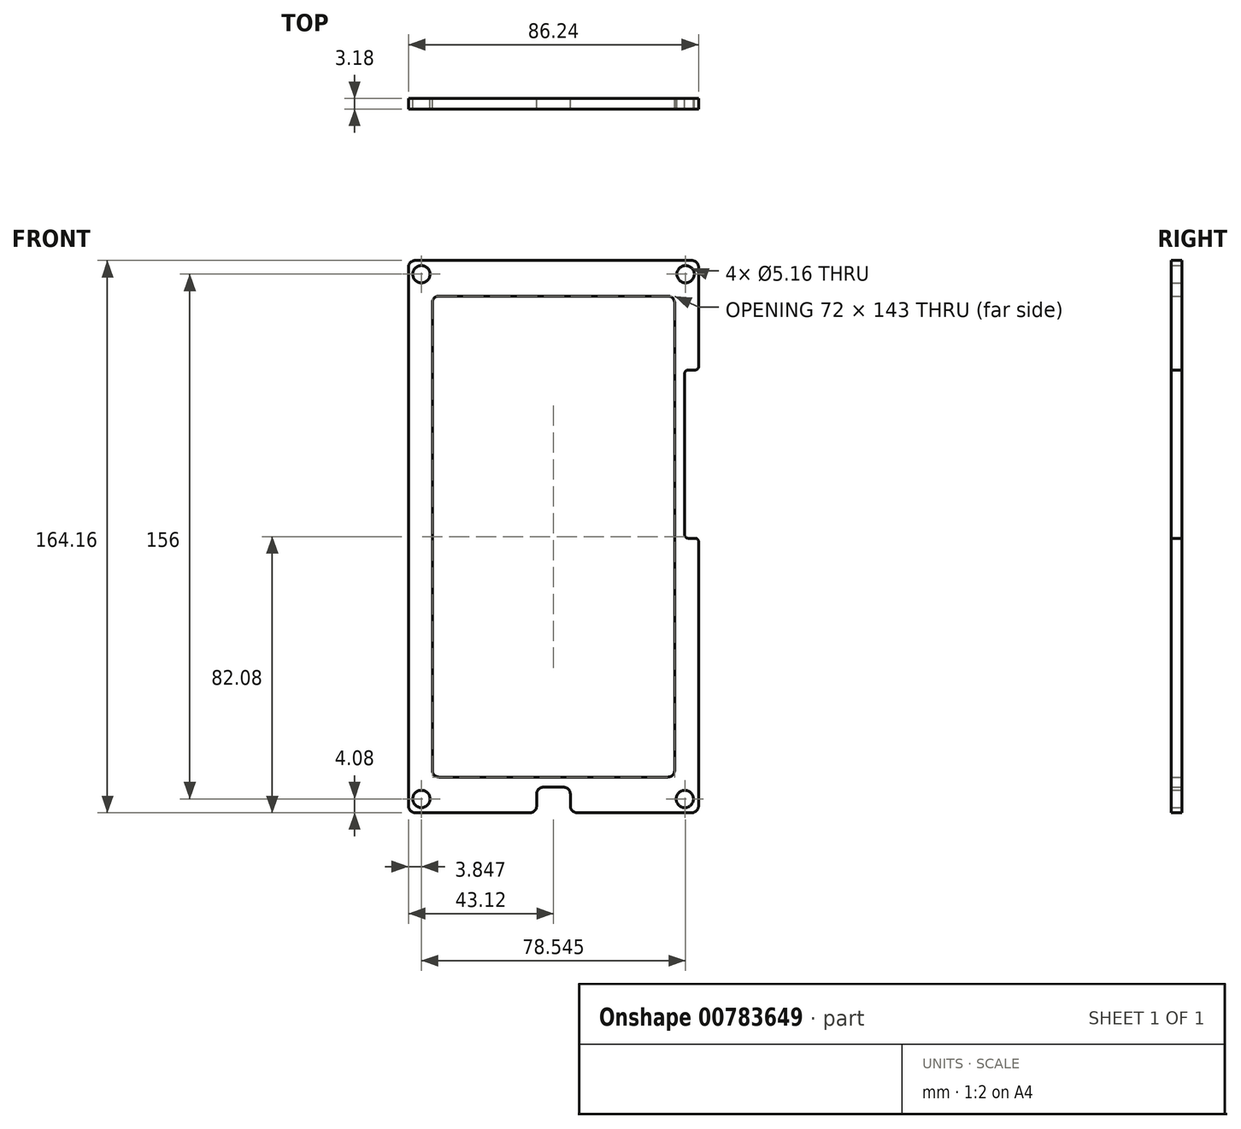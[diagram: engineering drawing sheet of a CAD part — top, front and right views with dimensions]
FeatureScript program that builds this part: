
annotation { "Feature Type Name" : "Feature", "Feature Type Description" : "" }
export const myFeature = defineFeature(function(context is Context, id is Id, definition is map)
    precondition{}
    {
        {
            var Q0;
            Q0=qCreatedBy(makeId("Front.planeOp"),FACE);
            var sketch = newSketch(context, id + "F0", { "sketchPlane" : qUnion([Q0])});
            skLineSegment(sketch, "E0.bottom", {"start": v(39, 74.5) * mm, "end": v(-39, 74.5) * mm});
            skLineSegment(sketch, "E0.top", {"start": v(39, -74.5) * mm, "end": v(-39, -74.5) * mm});
            skLineSegment(sketch, "E0.left", {"start": v(39, 74.5) * mm, "end": v(39, -74.5) * mm});
            skLineSegment(sketch, "E0.right", {"start": v(-39, 74.5) * mm, "end": v(-39, -74.5) * mm});
            skPoint(sketch, "E0.middle", {"position": v(0, 0) * mm});
            skSolve(sketch);
        }
        {
            var Q0;
            Q0=qCreatedBy(makeId("Front.planeOp"),FACE);
            var sketch = newSketch(context, id + "F1", { "sketchPlane" : qUnion([Q0])});
            skLineSegment(sketch, "E1.bottom", {"start": v(34, 71.5) * mm, "end": v(-34, 71.5) * mm});
            skLineSegment(sketch, "E1.top", {"start": v(34, -71.5) * mm, "end": v(-34, -71.5) * mm});
            skLineSegment(sketch, "E1.left", {"start": v(36, 69.5) * mm, "end": v(36, -69.5) * mm});
            skLineSegment(sketch, "E1.right", {"start": v(-36, 69.5) * mm, "end": v(-36, -69.5) * mm});
            skPoint(sketch, "E1.middle", {"position": v(0, 0) * mm});
            skCircle(sketch, "E2", {"center": v(39.27, 78) * mm, "radius": 2.58 * mm});
            skCircle(sketch, "E3", {"center": v(-39.27, 78) * mm, "radius": 2.58 * mm});
            skCircle(sketch, "E4", {"center": v(39.04, -78) * mm, "radius": 2.58 * mm});
            skCircle(sketch, "E5", {"center": v(-39.27, -78) * mm, "radius": 2.58 * mm});
            skLineSegment(sketch, "E6.bottom", {"start": v(41.12, 82.08) * mm, "end": v(-41.12, 82.08) * mm});
            skLineSegment(sketch, "E6.top", {"start": v(41.12, -82.08) * mm, "end": v(7, -82.08) * mm});
            skLineSegment(sketch, "E6.left", {"start": v(43.12, 80.08) * mm, "end": v(43.12, 50.5) * mm});
            skLineSegment(sketch, "E6.right", {"start": v(-43.12, 80.08) * mm, "end": v(-43.12, -80.08) * mm});
            skPoint(sketch, "E7.visualSharp", {"position": v(-36, 71.5) * mm});
            skArc(sketch, "E7.filletArc", {"start": v(-34, 71.5) * mm, "mid": v(-35.41, 70.91) * mm, "end": v(-36, 69.5) * mm});
            skPoint(sketch, "E8.visualSharp", {"position": v(36, 71.5) * mm});
            skArc(sketch, "E8.filletArc", {"start": v(36, 69.5) * mm, "mid": v(35.41, 70.91) * mm, "end": v(34, 71.5) * mm});
            skPoint(sketch, "E9.visualSharp", {"position": v(43.12, 82.08) * mm});
            skArc(sketch, "E9.filletArc", {"start": v(43.12, 80.08) * mm, "mid": v(42.53, 81.5) * mm, "end": v(41.12, 82.08) * mm});
            skPoint(sketch, "E10.visualSharp", {"position": v(-43.12, 82.08) * mm});
            skArc(sketch, "E10.filletArc", {"start": v(-41.12, 82.08) * mm, "mid": v(-42.53, 81.5) * mm, "end": v(-43.12, 80.08) * mm});
            skPoint(sketch, "E11.visualSharp", {"position": v(43.12, -82.08) * mm});
            skArc(sketch, "E11.filletArc", {"start": v(41.12, -82.08) * mm, "mid": v(42.53, -81.5) * mm, "end": v(43.12, -80.08) * mm});
            skPoint(sketch, "E12.visualSharp", {"position": v(36, -71.5) * mm});
            skArc(sketch, "E12.filletArc", {"start": v(34, -71.5) * mm, "mid": v(35.41, -70.91) * mm, "end": v(36, -69.5) * mm});
            skPoint(sketch, "E13.visualSharp", {"position": v(-43.12, -82.08) * mm});
            skArc(sketch, "E13.filletArc", {"start": v(-43.12, -80.08) * mm, "mid": v(-42.53, -81.5) * mm, "end": v(-41.12, -82.08) * mm});
            skPoint(sketch, "E14.visualSharp", {"position": v(-36, -71.5) * mm});
            skArc(sketch, "E14.filletArc", {"start": v(-36, -69.5) * mm, "mid": v(-35.41, -70.91) * mm, "end": v(-34, -71.5) * mm});
            skLineSegment(sketch, "E15.bottom", {"start": v(42.12, 49.5) * mm, "end": v(40, 49.5) * mm});
            skLineSegment(sketch, "E15.top", {"start": v(42.12, -0.5) * mm, "end": v(40, -0.5) * mm});
            skLineSegment(sketch, "E15.right", {"start": v(39, 48.5) * mm, "end": v(39, 0.5) * mm});
            skPoint(sketch, "E16.visualSharp", {"position": v(39, 49.5) * mm});
            skArc(sketch, "E16.filletArc", {"start": v(40, 49.5) * mm, "mid": v(39.3, 49.2) * mm, "end": v(39, 48.5) * mm});
            skPoint(sketch, "E17.visualSharp", {"position": v(39, -0.5) * mm});
            skArc(sketch, "E17.filletArc", {"start": v(39, 0.5) * mm, "mid": v(39.3, -0.2) * mm, "end": v(40, -0.5) * mm});
            skLineSegment(sketch, "E18.trimOffspring", {"start": v(43.12, -1.5) * mm, "end": v(43.12, -80.08) * mm});
            skPoint(sketch, "E19.visualSharp", {"position": v(43.12, -0.5) * mm});
            skArc(sketch, "E19.filletArc", {"start": v(43.12, -1.5) * mm, "mid": v(42.82, -0.8) * mm, "end": v(42.12, -0.5) * mm});
            skPoint(sketch, "E20.visualSharp", {"position": v(43.12, 49.5) * mm});
            skArc(sketch, "E20.filletArc", {"start": v(42.12, 49.5) * mm, "mid": v(42.82, 49.8) * mm, "end": v(43.12, 50.5) * mm});
            skLineSegment(sketch, "E21.top", {"start": v(-3, -74.5) * mm, "end": v(3, -74.5) * mm});
            skLineSegment(sketch, "E21.left", {"start": v(-5, -80.08) * mm, "end": v(-5, -76.5) * mm});
            skLineSegment(sketch, "E21.right", {"start": v(5, -80.08) * mm, "end": v(5, -76.5) * mm});
            skLineSegment(sketch, "E22.trimOffspring", {"start": v(-7, -82.08) * mm, "end": v(-41.12, -82.08) * mm});
            skPoint(sketch, "E23.visualSharp", {"position": v(-5, -74.5) * mm});
            skArc(sketch, "E23.filletArc", {"start": v(-3, -74.5) * mm, "mid": v(-4.41, -75.09) * mm, "end": v(-5, -76.5) * mm});
            skPoint(sketch, "E24.visualSharp", {"position": v(5, -74.5) * mm});
            skArc(sketch, "E24.filletArc", {"start": v(5, -76.5) * mm, "mid": v(4.41, -75.09) * mm, "end": v(3, -74.5) * mm});
            skPoint(sketch, "E25.visualSharp", {"position": v(5, -82.08) * mm});
            skArc(sketch, "E25.filletArc", {"start": v(5, -80.08) * mm, "mid": v(5.59, -81.5) * mm, "end": v(7, -82.08) * mm});
            skPoint(sketch, "E26.visualSharp", {"position": v(-5, -82.08) * mm});
            skArc(sketch, "E26.filletArc", {"start": v(-7, -82.08) * mm, "mid": v(-5.59, -81.5) * mm, "end": v(-5, -80.08) * mm});
            skSolve(sketch);
        }
        {
            var Q0;
            Q0 = qSketchRegion(id + "F1", true);
            extrude(context, id + "F2", {"entities" : qUnion([Q0]), "depth" : 3.17 * mm, "offsetDistance" : 25 * mm});
        }
    });
